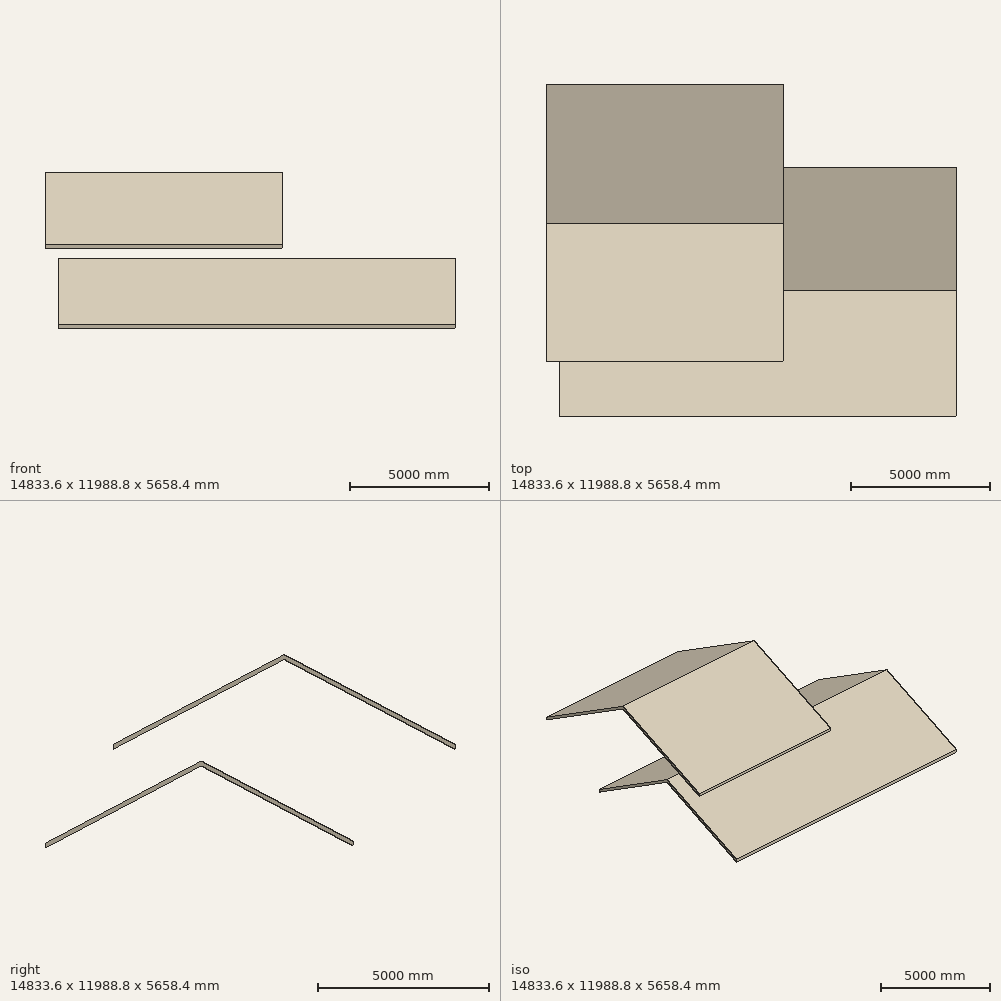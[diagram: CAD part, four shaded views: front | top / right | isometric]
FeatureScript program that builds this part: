
annotation { "Feature Type Name" : "Feature", "Feature Type Description" : "" }
export const myFeature = defineFeature(function(context is Context, id is Id, definition is map)
    precondition{}
    {
        {
            var Q0;
            Q0=qCreatedBy(makeId("Right.planeOp"),FACE);
            cPlane(context, id + "F0", {"entities" : qUnion([Q0]), "cplaneType" : CPlaneType.OFFSET, "offset" : 6248.4 * mm, "width" : 152.4 * mm, "height" : 152.4 * mm});
        }
        {
            var Q0;
            Q0=qCreatedBy(makeId("Right.planeOp"),FACE);
            cPlane(context, id + "F1", {"entities" : qUnion([Q0]), "cplaneType" : CPlaneType.OFFSET, "offset" : 7670.8 * mm, "oppositeDirection" : true, "width" : 152.4 * mm, "height" : 152.4 * mm});
        }
        {
            var Q0;
            Q0=qCreatedBy(makeId("Right.planeOp"),FACE);
            cPlane(context, id + "F2", {"entities" : qUnion([Q0]), "cplaneType" : CPlaneType.OFFSET, "offset" : 6705.6 * mm, "width" : 152.4 * mm, "height" : 152.4 * mm});
        }
        {
            var Q0;
            Q0=qCreatedBy(id+"F2.planeOp",FACE);
            var sketch = newSketch(context, id + "F3", { "sketchPlane" : qUnion([Q0])});
            skLineSegment(sketch, "E0", {"start": v(3340.1, 5372.1) * mm, "end": v(7772.4, 3035.58) * mm});
            skLineSegment(sketch, "E1.MirrorCS", {"start": v(3340.1, 5372.1) * mm, "end": v(-1219.2, 2968.64) * mm});
            skLineSegment(sketch, "E2.0", {"start": v(-1219.2, 2968.64) * mm, "end": v(-1219.2, 3112.2) * mm});
            skLineSegment(sketch, "E3.0", {"start": v(7772.4, 3035.58) * mm, "end": v(7772.4, 3179.15) * mm});
            skPoint(sketch, "E4.orphan", {"position": v(-635, 3276.6) * mm});
            skPoint(sketch, "E5.orphan", {"position": v(7315.2, 3276.6) * mm});
            skLineSegment(sketch, "E6.0", {"start": v(3340.1, 5515.67) * mm, "end": v(7772.4, 3179.15) * mm});
            skLineSegment(sketch, "E7.0", {"start": v(3340.1, 5515.67) * mm, "end": v(-1219.2, 3112.2) * mm});
            skSolve(sketch);
        }
        {
            var Q0;
            Q0=qCreatedBy(makeId("Right.planeOp"),FACE);
            cPlane(context, id + "F4", {"entities" : qUnion([Q0]), "cplaneType" : CPlaneType.OFFSET, "offset" : 8128 * mm, "oppositeDirection" : true, "width" : 152.4 * mm, "height" : 152.4 * mm});
        }
        {
            var Q0;
            Q0=qCreatedBy(id+"F4.planeOp",FACE);
            var sketch = newSketch(context, id + "F5", { "sketchPlane" : qUnion([Q0])});
            skLineSegment(sketch, "E8", {"start": v(10769.6, 5855.9) * mm, "end": v(5765.8, 8483.6) * mm});
            skLineSegment(sketch, "E9", {"start": v(5765.8, 8483.6) * mm, "end": v(762, 5855.9) * mm});
            skLineSegment(sketch, "E10.0", {"start": v(10769.6, 5999.35) * mm, "end": v(5765.8, 8627.05) * mm});
            skLineSegment(sketch, "E11.0", {"start": v(5765.8, 8627.05) * mm, "end": v(762, 5999.35) * mm});
            skLineSegment(sketch, "E12.0", {"start": v(10769.6, 5855.9) * mm, "end": v(10769.6, 5999.35) * mm});
            skLineSegment(sketch, "E13.0", {"start": v(762, 5855.9) * mm, "end": v(762, 5999.35) * mm});
            skSolve(sketch);
        }
        {
            var Q0;
            Q0=makeQuery(id+"F5.imprint","IMPRINT",FACE,{"disambiguationData":[TD([[makeQuery(id+"F5.imprint","IMPRINT",EDGE,{"derivedFrom":sQuery(id+"F5.wireOp",EDGE,"E8")}),-1.0]])]});
            extrude(context, id + "F6", {"entities" : qUnion([Q0]), "depth" : 8585.2 * mm});
        }
        {
            var Q0;
            Q0=makeQuery(id+"F3.imprint","IMPRINT",FACE,{"disambiguationData":[TD([[makeQuery(id+"F3.imprint","IMPRINT",EDGE,{"derivedFrom":sQuery(id+"F3.wireOp",EDGE,"E0")}),1.0]])]});
            extrude(context, id + "F7", {"entities" : qUnion([Q0]), "oppositeDirection" : true, "depth" : 14376.4 * mm});
        }
    });
